# Revit family: Bath-Waterworks-Minna-Rectangular
name_source: partatom
category: Plumbing Fixtures
revit_build: Autodesk Revit MEP 2014 (Build: 20140709_2115(x64)
units: mm (PartAtom-declared; Revit-internal decimal feet)

## types (4) — shared parameters
ADA Compliant = No
Assembly Code = D2010510
CW Connection = No
Code Compliance = Code # WWBT70:
Default Elevation = 0' - 0"
Depth = 2' - 6"
Depth to Overflow = 1' - 2 5/16"
Drain Hole Diameter = 0' - 2 1/16"
Finish = Enameled, Cast Iron - Waterworks -  White
HW Connection = No
Height = 1' - 8"
Length = 5' - 0"
Manufacturer = Waterworks
Model = MIBT70
Overflow Hole Diameter = 0' - 2 1/16"
Product Documentation Link = http://assets.waterworks.com
Product Page URL = http://www.waterworks.com
Sanitary Connector = Sanitary Connector
URL = http://www.waterworks.com
Vent Connection = No
Version = 2014 - v1.0a
Warranty = http://www.waterworks.com
Waste Connection = Yes
Water Capacity = 55 Gallons
‌Installation Requirements or Notes = Dimensions of fixtures are nominal. Measure your actual product for rough-in details.
zero-valued in all types: CWFU, HWFU, WFU

## per-type parameters (varying)
| type | Constraint | DUBT6L | DUBT6R | Description | Keynote | Model SKU | Product Name |
| Rectangular-End Drain in White | 1 | Yes | No | Minna Rectangular Cast Iron Bathtub with End Drain in White | 22 40 00.D2 | 13-82588-26711 | Minna 60” x 30” x 20” Rectangular Cast Iron Bathtub with End Drain in White |
| Rectangular-Slip Resistance in White | 2 | No | Yes | Minna Rectangular Cast Iron Bathtub with Slip Resistance in White | 22 40 00 | 13-98481-96189 | Minna 60” x 30” x 20” Rectangular Cast Iron Bathtub with Slip Resistance in White |
| Undermount Rectangular-White | 3 | No | Yes | Minna Undermount Only Rectangular Cast Iron Bathtub in White | 22 40 00 | 13-00203-95734 | Minna 60” x 30” x 20” Undermount Only Rectangular Cast Iron Bathtub in White |
| Undermount Rectangular-End Drain and Slip Resistance in White | 4 | No | Yes | Minna Undermount Only Rectangular Cast Iron Bathtub with End Drain and Slip Resistance in White | 22 40 00 | 13-32069-90882 | Minna 60” x 30” x 20” Undermount Only Rectangular Cast Iron Bathtub with End Drain and Slip Resistance in White |

## geometry (parser evidence)
native form markers: Sweep x6
no freeform markers — native parametric forms only
